SOLIDWORKS PART (.sldprt)
format: sldprt  version: not decoded by parser v0  size: 235,008 bytes
history: native  units: mm
features: plane x8, sketch x6, extrude x3, material x1, mirror x1, cut_extrude x1, pattern_circular x1 (+13 scaffold rows collapsed)
feature tree (34):
  scaffold x13  (default folders/planes/origin — collapsed)
  material  "材质 <未指定>"
  plane  "前视基准面"
  plane  "上视基准面"
  plane  "右视基准面"
  plane  "基准面1"  Offset=1025mm
  sketch  "草图1"  dims[D1=100.0mm D2=180.0mm]
  extrude  "凸台-拉伸1"  Depth=100mm
  plane  "基准面2"  Offset=150mm
  plane  "基准面3"  Offset=150mm
  sketch  "草图4"  dims[D1=500.0mm]
  plane  "基准面4"  Offset=50mm
  plane  "基准面5"  Offset=50mm
  sketch  "草图5"  dims[D1=300.0mm]
  sketch  "草图6"  dims[D1=300.0mm]
  extrude  "凸台-拉伸2"  Depth=100mm
  sketch  "草图8"  dims[D1=450.0mm]
  extrude  "凸台-拉伸4"  Depth=300mm
  mirror  "镜向2"
  sketch  "草图9"  dims[D1=0.0mm]
  cut_extrude  "切除-拉伸1"  Depth=5mm
  pattern_circular  "阵列(圆周)1"  Count=12 Angle=30deg
decode coverage: 11 of 12 modeling features carry decoded parameters
note: suppression state not decoded; provenance and decode notes live in map.json
